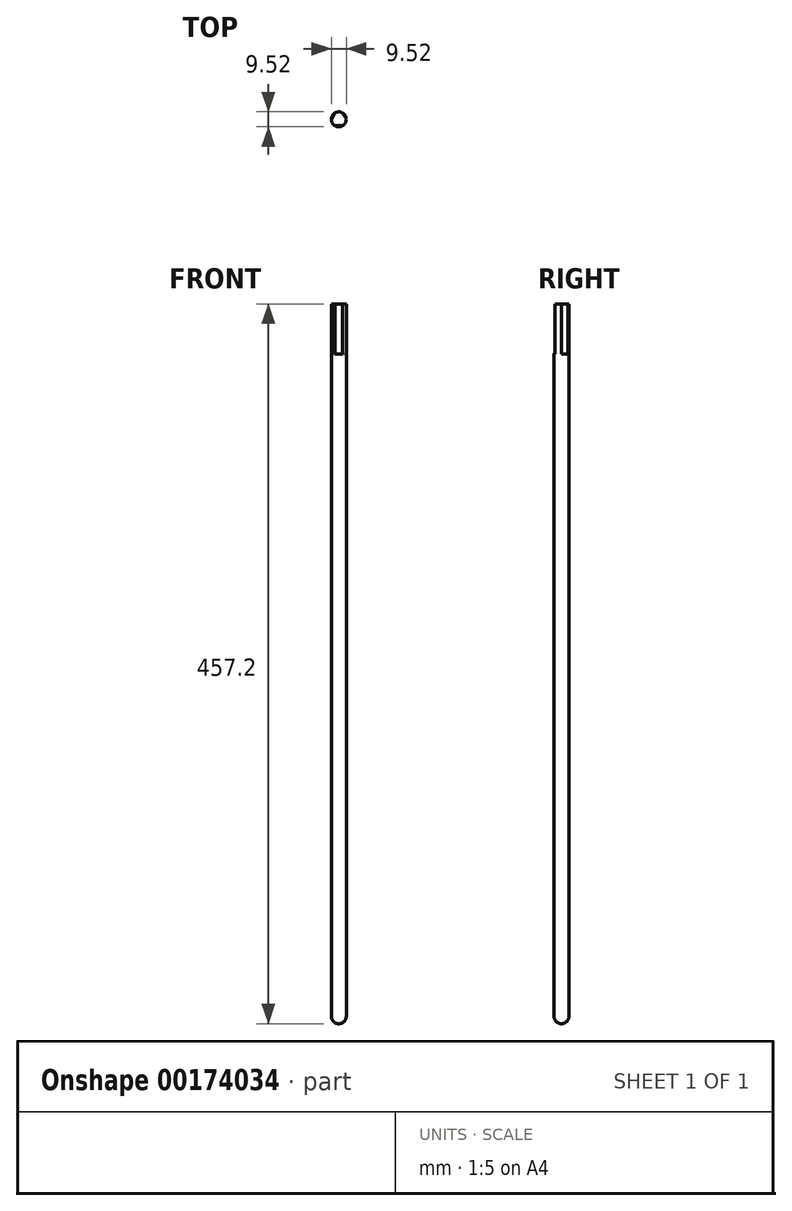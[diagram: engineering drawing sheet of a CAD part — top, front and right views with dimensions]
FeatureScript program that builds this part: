
annotation { "Feature Type Name" : "Feature", "Feature Type Description" : "" }
export const myFeature = defineFeature(function(context is Context, id is Id, definition is map)
    precondition{}
    {
        {
            var Q0;
            Q0=qCreatedBy(makeId("Top.planeOp"),FACE);
            var sketch = newSketch(context, id + "F3", { "sketchPlane" : qUnion([Q0])});
            skCircle(sketch, "E0", {"center": v(0, 0) * mm, "radius": 4.76 * mm});
            skLineSegment(sketch, "E1", {"start": v(2.38, -4.13) * mm, "end": v(-2.38, -4.13) * mm});
            skLineSegment(sketch, "E2", {"start": v(2.44, 4.09) * mm, "end": v(4.76, 0.07) * mm});
            skLineSegment(sketch, "E3", {"start": v(-4.76, 0) * mm, "end": v(-2.39, 4.12) * mm});
            skSolve(sketch);
        }
        {
            var Q0;
            {var subQ0=sQuery(id+"F3.wireOp",EDGE,"E1");Q0=makeQuery(id+"F3.imprint","IMPRINT",FACE,{"disambiguationData":[TD([[makeQuery(id+"F3.imprint","IMPRINT",EDGE,{"derivedFrom":subQ0}),-1.0]])]});}
            extrude(context, id + "F0", {"entities" : qUnion([Q0]), "depth" : 31.75 * mm});
        }
        {
            var Q0;
            Q0 = qSketchRegion(id + "F3", true);
            extrude(context, id + "F1", {"entities" : qUnion([Q0]), "operationType" : NewBodyOperationType.ADD, "oppositeDirection" : true, "depth" : 425.45 * mm});
        }
        {
            var Q0;
            Q0=makeQuery(id+"F1.opExtrude","CAP_FACE",FACE,{"disambiguationData":[OSD([sQuery(id+"F3.wireOp",EDGE,"E0")])],"isStart":false});
            fillet(context, id + "F2", {"entities" : qUnion([Q0]), "radius" : 4.76 * mm, "tangentPropagation" : true, "allowEdgeOverflow" : false});
        }
    });
